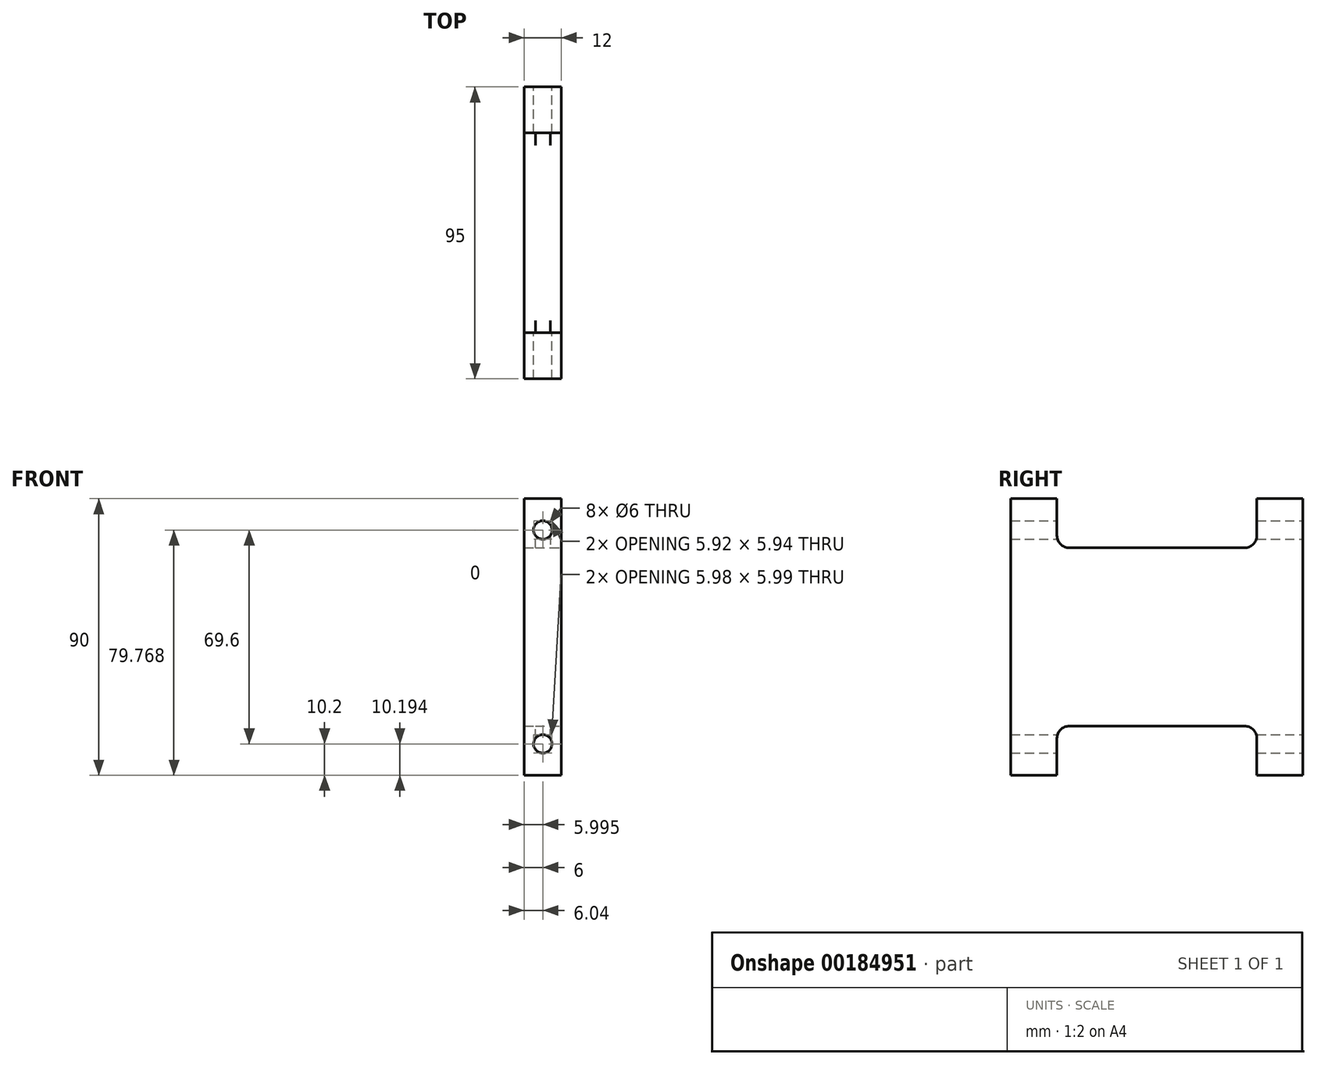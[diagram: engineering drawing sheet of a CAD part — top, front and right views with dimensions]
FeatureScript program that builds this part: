
annotation { "Feature Type Name" : "Feature", "Feature Type Description" : "" }
export const myFeature = defineFeature(function(context is Context, id is Id, definition is map)
    precondition{}
    {
        {
            var Q0;
            Q0=qCreatedBy(makeId("Front.planeOp"),FACE);
            var sketch = newSketch(context, id + "F0", { "sketchPlane" : qUnion([Q0])});
            skLineSegment(sketch, "E0.bottom", {"start": v(0, -45) * mm, "end": v(12, -45) * mm});
            skLineSegment(sketch, "E0.top", {"start": v(0, 45) * mm, "end": v(12, 45) * mm});
            skLineSegment(sketch, "E0.left", {"start": v(0, -45) * mm, "end": v(0, 45) * mm});
            skLineSegment(sketch, "E0.right", {"start": v(12, -45) * mm, "end": v(12, 45) * mm});
            skCircle(sketch, "E1", {"center": v(6, 34.8) * mm, "radius": 3 * mm});
            skCircle(sketch, "E2.MirrorC", {"center": v(6, -34.8) * mm, "radius": 3 * mm});
            skSolve(sketch);
        }
        {
            var Q0;
            Q0 = qSketchRegion(id + "F0", true);
            extrude(context, id + "F1", {"entities" : qUnion([Q0]), "depth" : 95 * mm});
        }
        {
            var Q0;
            Q0=makeQuery(id+"F1.opExtrude","SWEPT_FACE",FACE,{"disambiguationData":[OSD([sQuery(id+"F0.wireOp",EDGE,"E0.right")])]});
            var sketch = newSketch(context, id + "F4", { "sketchPlane" : qUnion([Q0])});
            skLineSegment(sketch, "E3", {"start": v(-80, 45) * mm, "end": v(-80, 29) * mm});
            skLineSegment(sketch, "E4", {"start": v(-80, 29) * mm, "end": v(-15, 29) * mm});
            skLineSegment(sketch, "E5", {"start": v(-15, 29) * mm, "end": v(-15, 45) * mm});
            skLineSegment(sketch, "E6", {"start": v(-15, 45) * mm, "end": v(-80, 45) * mm});
            skLineSegment(sketch, "E7", {"start": v(-69.22, 0) * mm, "end": v(-69.22, 0) * mm});
            skLineSegment(sketch, "E8.MirrorCS", {"start": v(-15, -45) * mm, "end": v(-80, -45) * mm});
            skLineSegment(sketch, "E9.MirrorCS", {"start": v(-15, -29) * mm, "end": v(-15, -45) * mm});
            skLineSegment(sketch, "E10.MirrorCS", {"start": v(-80, -29) * mm, "end": v(-15, -29) * mm});
            skLineSegment(sketch, "E11.MirrorCS", {"start": v(-80, -45) * mm, "end": v(-80, -29) * mm});
            skPoint(sketch, "E12.end.orphan", {"position": v(-95, 0) * mm});
            skSolve(sketch);
        }
        {
            var Q0;
            Q0=makeQuery(id+"F4.imprint","IMPRINT",FACE,{"disambiguationData":[TD([[makeQuery(id+"F4.imprint","IMPRINT",EDGE,{"derivedFrom":sQuery(id+"F4.wireOp",EDGE,"E8.MirrorCS")}),1.0]])]});
            var Q1;
            Q1=makeQuery(id+"F4.imprint","IMPRINT",FACE,{"disambiguationData":[TD([[makeQuery(id+"F4.imprint","IMPRINT",EDGE,{"derivedFrom":sQuery(id+"F4.wireOp",EDGE,"E3")}),1.0]])]});
            extrude(context, id + "F2", {"entities" : qUnion([Q0, Q1]), "operationType" : NewBodyOperationType.REMOVE, "endBound" : BoundingType.THROUGH_ALL, "oppositeDirection" : true, "depth" : 25 * mm});
        }
        {
            var Q0;
            Q0=makeQuery(id+"F2.boolean.opBoolean","COPY",EDGE,{"derivedFrom":makeQuery(id+"F2.opExtrude","SWEPT_EDGE",EDGE,{"disambiguationData":[OSD([sQuery(id+"F4.wireOp",EDGE,"E10.MirrorCS"),sQuery(id+"F4.wireOp",EDGE,"E11.MirrorCS")])]})});
            var Q1;
            Q1=makeQuery(id+"F2.boolean.opBoolean","COPY",EDGE,{"derivedFrom":makeQuery(id+"F2.opExtrude","SWEPT_EDGE",EDGE,{"disambiguationData":[OSD([sQuery(id+"F4.wireOp",EDGE,"E9.MirrorCS"),sQuery(id+"F4.wireOp",EDGE,"E10.MirrorCS")])]})});
            var Q2;
            Q2=makeQuery(id+"F2.boolean.opBoolean","COPY",EDGE,{"derivedFrom":makeQuery(id+"F2.opExtrude","SWEPT_EDGE",EDGE,{"disambiguationData":[OSD([sQuery(id+"F4.wireOp",EDGE,"E4"),sQuery(id+"F4.wireOp",EDGE,"E5")])]})});
            var Q3;
            Q3=makeQuery(id+"F2.boolean.opBoolean","COPY",EDGE,{"derivedFrom":makeQuery(id+"F2.opExtrude","SWEPT_EDGE",EDGE,{"disambiguationData":[OSD([sQuery(id+"F4.wireOp",EDGE,"E3"),sQuery(id+"F4.wireOp",EDGE,"E4")])]})});
            fillet(context, id + "F3", {"entities" : qUnion([Q0, Q1, Q2, Q3]), "radius" : 4 * mm, "tangentPropagation" : true, "allowEdgeOverflow" : false});
        }
    });
